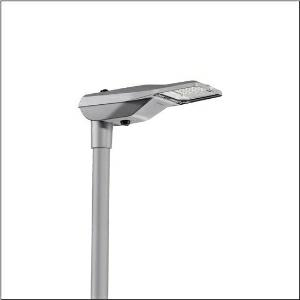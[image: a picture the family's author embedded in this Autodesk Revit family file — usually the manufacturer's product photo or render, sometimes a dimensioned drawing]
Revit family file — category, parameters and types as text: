
# Revit family: streetlight_sl_21_iq_micro___st1_0a_5xe1d21y08cb_9119
name_source: partatom
category: Lighting Fixtures
units: mm (PartAtom-declared; Revit-internal decimal feet)

## family parameters
Cut with Voids When Loaded = No
Host = Face
Light Source = No
Part Type = Normal
Room Calculation Point = No
Round Connector Dimension = Use Diameter
Shared = No

## types (1)
- --- (1 x LED, 2310 lm, 19.1 W, 2200K)
    Apparent Load = 19 VA
    CIE Flux Codes = 37 72 97 100 100
    Color Rendering = 70
    Color Temperature = 2200K
    Default Elevation = 1800 mm
    Description = Streetlight SL 21 iQ micro, mast luminaire, primary light control with lens, of PMMA, primary optical cover: cover, of toughened safety glass, transparent, light distribution: ST1.0a, light emission: direct distribution, primary light characteristic: asymmetric, installation type: post-top, side-entry, LED, High Power LED, rated luminous flux: 2.310lm, luminous efficacy: 121lm/W, light colour: 722, colour temperature: 2200K, control gear: iQ-Street Remote, D4i with power reduction, control: pre-setting: logarithmic dimming characteristic, Street-Remote, Auto-Match, Temp-Guard, Lumen-Switch, Night-Set, Smart-Wire, Light-Fading, Desk-Remote (wireless, voltage-free reading and setting of iQ features in the workshop via application-optimized NFC function/RFID function), optimised constant luminous flux control (CLO 2.0), mains connection: 220..240V, AC, 50/60Hz, start of lifetime: 19W, end of service life: 20W, reduction: 9W, luminaire housing, of diecast aluminium, powder-coated, Siteco® metallic grey (DB 702S), corrosivity category C5 mid according to DIN EN ISO 12944, please order mast flange separately, inclination adjustable: 0°, 5°, 10°, 15°, sealing non-destructively replaceable, multi-level sealing system, length: 528mm, width: 235mm, height: 110mm, mast flange for spigot size: 42mm (side-entry): 5XC10008XM4, 60/48mm (side-entry/post-top): 5XC10108XM2, 76/60mm (side-entry/post-top): 5XC10108XM1, mounting height: 4..8m, Smart Interface below and above, protection rating (complete): IP66, insulation class (complete): insulation class II (safety insulation), certification: CE, ENEC, ENEC+, VDE, impact resistance: IK10, permissible operating ambient temperature for outdoor applications: -40..+50°C, standard-compliant lighting for roads and squares, packaging unit: 1 piece

Light Distribution: ST1.0a
    Height = 110 mm
    Lamp = 1 x LED
    Lamp Light Flux = 2310 lm
    Lamp Power = 19.1 W
    Lamp count = 1
    Length = 528 mm
    Luminous efficacy = 121 lm/W
    Manufacturer = Siteco
    ModVariant = No
    Model = 5XE1D21Y08CB
    Number of Poles = 1
    OnlyDefault = Yes
    Power Factor = 1
    Product Name = Streetlight SL 21 iQ micro | ST1.0a
    Product group = mast luminaire | pylon top
    ProductGroupID = 6100
    Protection Class = Protection class II
    Protection Degree = IP 66
    RLX_Detail_Level = 1
    RLX_Emergency_Light_Flux = 0 lm
    RLX_Emergency_Type = 0
    RLX_Emergency_Type_DB = No
    RlxData = <blob elided: 98857 chars, md5=da182808>
    Socket = socket
    Standby Power = 0 W
    System Light Flux = 2310 lm
    System Power = 19 W
    Type Comments = factory setting: luminous flux: 100 % | dim-lin: 254 | 387 mA
    Type Image = l_1007239.jpg
    URL = http://relux.com
    VarID = @adj_137085
    Voltage = 0 V
    Weight = 0.00 kg
    Width = 235 mm

## geometry (parser evidence)
native form markers: Blend x4, Sweep x9
no freeform markers — native parametric forms only
